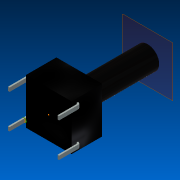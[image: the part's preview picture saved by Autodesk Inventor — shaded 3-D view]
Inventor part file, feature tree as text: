
AUTODESK INVENTOR PART (.ipt)
format: ipt  version: 2015 SP1 (Build 190203100, 203)  size: 144,896 bytes
history: native  units: mm
features: sketch x7, projected_geometry x3, other x2, sweep x2, extrude x1, loft x1
ambient origin geometry x8: Origin, YZ Plane, XZ Plane, XY Plane, X Axis, Y Axis, Z Axis, Center Point
bodies: Body1 (feature_tree)
feature tree (16):
  other  "Твердое тело1"
  extrude  "Выдавливание1"  Depth=6.0mm
  sketch  "Эскиз2"
  other  "РабПлоскость1"
  loft  "Лофт1"
  sketch  "Эскиз4"
  sketch  "Эскиз5"
  sketch  "Эскиз6"
  sweep  "Сдвиг1"
  sweep  "Сдвиг2"
  sketch  "Эскиз7"
  sketch  "Эскиз1"
  sketch  "Эскиз3"
  projected_geometry  "Спроецированная петля1"
  projected_geometry  "Спроецированная петля2"
  projected_geometry  "Спроецированная петля3"
